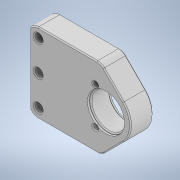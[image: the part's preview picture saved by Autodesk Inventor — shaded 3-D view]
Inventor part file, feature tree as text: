
AUTODESK INVENTOR PART (.ipt)
format: ipt  version: 2020 (Build 240168000, 168)  size: 254,464 bytes
history: native  units: in
note: dims shown in document units (in); Inventor stores cm internally (conversion verified against a paired STEP export)
features: extrude x4, sketch x4, chamfer x2, fillet x1
ambient origin geometry x8: Origin, YZ Plane, XZ Plane, XY Plane, X Axis, Y Axis, Z Axis, Center Point
bodies: Solid1 (feature_tree)
feature tree (11):
  extrude  "Extrusion1"  Depth=1.0in
  fillet  "Fillet1"  Radius=0.2656in
  extrude  "Extrusion2"  Depth=0.3198in
  extrude  "Extrusion3"  Depth=0.3198in
  extrude  "Extrusion4"  TaperAngle=45.0deg  [1 undecoded]
  chamfer  "Chamfer1"  Angle=45.0deg  [1 undecoded]
  chamfer  "Chamfer2"  Distance=0.75in
  sketch  "Sketch1"  dims[d0=1.126in d1=1.0in d2=0.2656in]
  sketch  "Sketch2"  dims[d4=1.1811in d6=1.0in d7=0.3937in d9=1.0in d11=0.3198in]
  sketch  "Sketch3"  dims[d12=0.3198in d13=0.3198in]
  sketch  "Sketch4"  dims[d14=0.813in d15=45.0deg d16=45.0deg d17=0.75in d18=0.0in d19=0.3198in d20=0.7105in d21=0.159in d22=120.0deg d23=1.1811in d25=360.0deg d27=0.0in d28=0.0in d29=1.226in d30=0.064in d31=0.0in d32=1.226in d33=0.064in d34=0.0in d35=0.035in d36=0.125in d37=45.0deg d43=1.225in d45=2.25in d46=1.6375in d47=2.0in d48=1.0in d49=135.0deg d50=0.375in d51=0.125in d52=0.125in d53=45.0deg]
note: 2 required parameter values undecoded (feature->parameter linkage not recoverable at this tier; creation-order binding heuristic only, values carry confidence <= 0.55)
